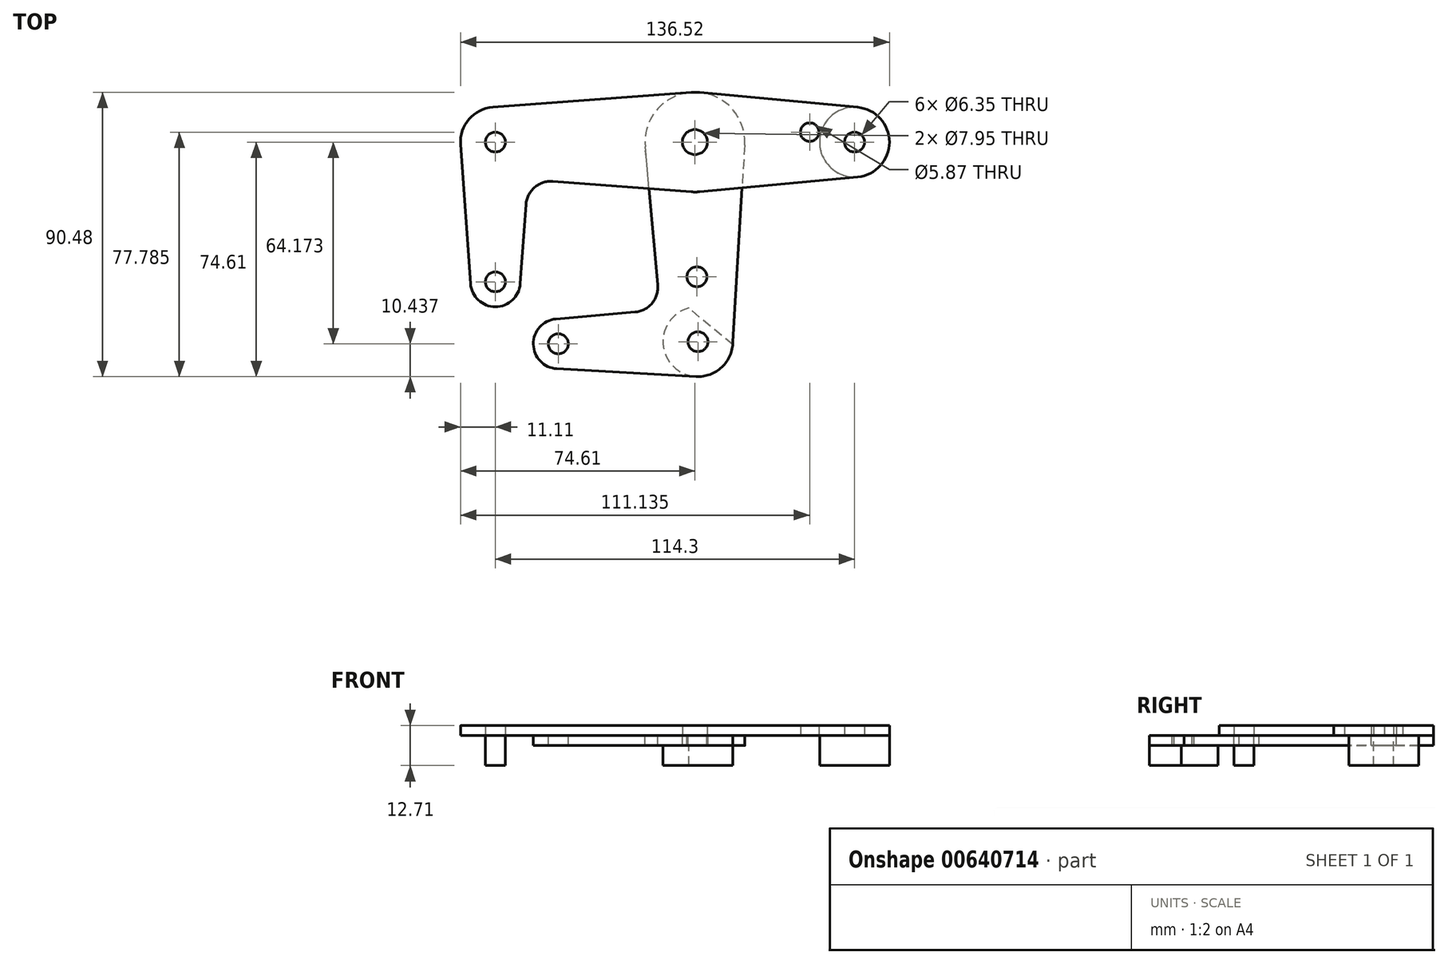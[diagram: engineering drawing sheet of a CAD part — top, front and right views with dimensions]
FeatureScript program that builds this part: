
annotation { "Feature Type Name" : "Feature", "Feature Type Description" : "" }
export const myFeature = defineFeature(function(context is Context, id is Id, definition is map)
    precondition{}
    {
        {
            var Q0;
            Q0=qCreatedBy(makeId("Top.planeOp"),FACE);
            var sketch = newSketch(context, id + "F0", { "sketchPlane" : qUnion([Q0])});
            skCircle(sketch, "E0", {"center": v(-63.5, -44.45) * mm, "radius": 3.18 * mm});
            skCircle(sketch, "E1", {"center": v(-63.5, -44.45) * mm, "radius": 7.94 * mm});
            skCircle(sketch, "E2", {"center": v(-63.5, 0) * mm, "radius": 3.18 * mm});
            skCircle(sketch, "E3", {"center": v(-63.5, 0) * mm, "radius": 11.11 * mm});
            skCircle(sketch, "E4", {"center": v(0, 0) * mm, "radius": 2.94 * mm});
            skCircle(sketch, "E5", {"center": v(0, 0) * mm, "radius": 3.98 * mm});
            skCircle(sketch, "E6", {"center": v(0, 0) * mm, "radius": 15.88 * mm});
            skLineSegment(sketch, "E7", {"start": v(-71.42, -45.02) * mm, "end": v(-74.58, -0.8) * mm});
            skLineSegment(sketch, "E8", {"start": v(-64.33, 11.08) * mm, "end": v(-1.2, 15.83) * mm});
            skLineSegment(sketch, "E9", {"start": v(-53.78, -19.88) * mm, "end": v(-55.58, -45.02) * mm});
            skLineSegment(sketch, "E10", {"start": v(-1.2, -15.83) * mm, "end": v(-45.26, -12.52) * mm});
            skArc(sketch, "E11", {"start": v(-45.26, -12.52) * mm, "mid": v(-51.05, -14.43) * mm, "end": v(-53.78, -19.88) * mm});
            skLineSegment(sketch, "E12", {"start": v(-63.5, 0) * mm, "end": v(-63.5, -44.45) * mm, "construction": true});
            skCircle(sketch, "E13", {"center": v(0.96, -63.5) * mm, "radius": 11.11 * mm});
            skCircle(sketch, "E14", {"center": v(0.96, -63.5) * mm, "radius": 3.18 * mm});
            skCircle(sketch, "E15", {"center": v(-43.49, -64.17) * mm, "radius": 7.94 * mm});
            skCircle(sketch, "E16", {"center": v(-43.49, -64.17) * mm, "radius": 3.18 * mm});
            skLineSegment(sketch, "E17", {"start": v(15.85, -0.96) * mm, "end": v(12.07, -63.5) * mm});
            skLineSegment(sketch, "E18", {"start": v(0.34, -74.6) * mm, "end": v(-43.94, -72.1) * mm});
            skCircle(sketch, "E19", {"center": v(0.65, -42.85) * mm, "radius": 3.18 * mm});
            skLineSegment(sketch, "E20", {"start": v(0, 0) * mm, "end": v(0.96, -63.5) * mm, "construction": true});
            skLineSegment(sketch, "E21", {"start": v(0.96, -63.5) * mm, "end": v(-43.49, -64.17) * mm, "construction": true});
            skLineSegment(sketch, "E22", {"start": v(-63.5, 0) * mm, "end": v(50.8, 0) * mm, "construction": true});
            skCircle(sketch, "E23", {"center": v(50.8, 0) * mm, "radius": 11.11 * mm});
            skLineSegment(sketch, "E24", {"start": v(1.49, 15.8) * mm, "end": v(51.84, 11.06) * mm});
            skLineSegment(sketch, "E25", {"start": v(1.49, -15.8) * mm, "end": v(51.84, -11.06) * mm});
            skCircle(sketch, "E26", {"center": v(36.53, 3.17) * mm, "radius": 2.94 * mm});
            skLineSegment(sketch, "E27", {"start": v(36.53, 0) * mm, "end": v(36.53, 3.17) * mm, "construction": true});
            skCircle(sketch, "E28", {"center": v(50.8, 0) * mm, "radius": 3.18 * mm});
            skLineSegment(sketch, "E29", {"start": v(0, -52.43) * mm, "end": v(0, -52.43) * mm});
            skArc(sketch, "E30", {"start": v(-19.06, -54.08) * mm, "mid": v(-13.65, -51.27) * mm, "end": v(-11.83, -45.45) * mm});
            skLineSegment(sketch, "E31.trimOffspring", {"start": v(-19.06, -54.08) * mm, "end": v(-44.18, -56.27) * mm});
            skLineSegment(sketch, "E32", {"start": v(-11.83, -45.45) * mm, "end": v(-15.81, -1.43) * mm});
            skSolve(sketch);
        }
        {
            var Q0;
            {var subQ0=sQuery(id+"F0.wireOp",EDGE,"E10");var subQ1=sQuery(id+"F0.wireOp",EDGE,"E6");var subQ2=makeQuery(id+"F0.imprint","INTERSECT",VERTEX,{"derivedFrom":[subQ1,subQ0]});Q0=makeQuery(id+"F0.imprint","IMPRINT",FACE,{"disambiguationData":[TD([[makeQuery(id+"F0.imprint","IMPRINT",EDGE,{"disambiguationData":[TD([[subQ2,1.0]])],"derivedFrom":subQ1}),-1.0]])]});}
            var Q1;
            Q1=makeQuery(id+"F0.imprint","IMPRINT",FACE,{"disambiguationData":[TD([[makeQuery(id+"F0.imprint","IMPRINT",EDGE,{"derivedFrom":sQuery(id+"F0.wireOp",EDGE,"E5")}),-1.0]])]});
            var Q2;
            {var subQ0=sQuery(id+"F0.wireOp",EDGE,"E17");var subQ1=sQuery(id+"F0.wireOp",EDGE,"E6");var subQ2=makeQuery(id+"F0.imprint","INTERSECT",VERTEX,{"derivedFrom":[subQ1,subQ0]});Q2=makeQuery(id+"F0.imprint","IMPRINT",FACE,{"disambiguationData":[TD([[makeQuery(id+"F0.imprint","IMPRINT",EDGE,{"disambiguationData":[TD([[subQ2,1.0]])],"derivedFrom":subQ1}),-1.0]])]});}
            var Q3;
            {var subQ0=sQuery(id+"F0.wireOp",EDGE,"E24");Q3=makeQuery(id+"F0.imprint","IMPRINT",FACE,{"disambiguationData":[TD([[makeQuery(id+"F0.imprint","IMPRINT",EDGE,{"derivedFrom":subQ0}),-1.0]])]});}
            var Q4;
            Q4=makeQuery(id+"F0.imprint","IMPRINT",FACE,{"disambiguationData":[TD([[makeQuery(id+"F0.imprint","IMPRINT",EDGE,{"derivedFrom":sQuery(id+"F0.wireOp",EDGE,"E28")}),-1.0]])]});
            var Q5;
            {var subQ0=sQuery(id+"F0.wireOp",EDGE,"E7");Q5=makeQuery(id+"F0.imprint","IMPRINT",FACE,{"disambiguationData":[TD([[makeQuery(id+"F0.imprint","IMPRINT",EDGE,{"derivedFrom":subQ0}),-1.0]])]});}
            var Q6;
            Q6=makeQuery(id+"F0.imprint","IMPRINT",FACE,{"disambiguationData":[TD([[makeQuery(id+"F0.imprint","IMPRINT",EDGE,{"derivedFrom":sQuery(id+"F0.wireOp",EDGE,"E0")}),-1.0]])]});
            var Q7;
            Q7=makeQuery(id+"F0.imprint","IMPRINT",FACE,{"disambiguationData":[TD([[makeQuery(id+"F0.imprint","IMPRINT",EDGE,{"derivedFrom":sQuery(id+"F0.wireOp",EDGE,"E2")}),-1.0]])]});
            extrude(context, id + "F1", {"entities" : qUnion([Q0, Q1, Q2, Q3, Q4, Q5, Q6, Q7]), "depth" : 3.17 * mm, "offsetDistance" : 25.4 * mm});
        }
        {
            var Q0;
            {var subQ11=sQuery(id+"F0.wireOp",EDGE,"E18");Q0=makeQuery(id+"F0.imprint","IMPRINT",FACE,{"disambiguationData":[TD([[makeQuery(id+"F0.imprint","IMPRINT",EDGE,{"derivedFrom":subQ11}),-1.0]])]});}
            var Q1;
            Q1=makeQuery(id+"F0.imprint","IMPRINT",FACE,{"disambiguationData":[TD([[makeQuery(id+"F0.imprint","IMPRINT",EDGE,{"derivedFrom":sQuery(id+"F0.wireOp",EDGE,"E14")}),-1.0]])]});
            var Q2;
            Q2=makeQuery(id+"F0.imprint","IMPRINT",FACE,{"disambiguationData":[TD([[makeQuery(id+"F0.imprint","IMPRINT",EDGE,{"derivedFrom":sQuery(id+"F0.wireOp",EDGE,"E16")}),-1.0]])]});
            var Q3;
            {var subQ0=sQuery(id+"F0.wireOp",EDGE,"E17");var subQ1=sQuery(id+"F0.wireOp",EDGE,"E6");var subQ2=makeQuery(id+"F0.imprint","INTERSECT",VERTEX,{"derivedFrom":[subQ1,subQ0]});Q3=makeQuery(id+"F0.imprint","IMPRINT",FACE,{"disambiguationData":[TD([[makeQuery(id+"F0.imprint","IMPRINT",EDGE,{"disambiguationData":[TD([[subQ2,1.0]])],"derivedFrom":subQ1}),-1.0]])]});}
            var Q4;
            Q4=makeQuery(id+"F0.imprint","IMPRINT",FACE,{"disambiguationData":[TD([[makeQuery(id+"F0.imprint","IMPRINT",EDGE,{"derivedFrom":sQuery(id+"F0.wireOp",EDGE,"E5")}),-1.0]])]});
            var Q5;
            {var subQ0=sQuery(id+"F0.wireOp",EDGE,"E10");var subQ1=sQuery(id+"F0.wireOp",EDGE,"E6");var subQ2=makeQuery(id+"F0.imprint","INTERSECT",VERTEX,{"derivedFrom":[subQ1,subQ0]});Q5=makeQuery(id+"F0.imprint","IMPRINT",FACE,{"disambiguationData":[TD([[makeQuery(id+"F0.imprint","IMPRINT",EDGE,{"disambiguationData":[TD([[subQ2,1.0]])],"derivedFrom":subQ1}),-1.0]])]});}
            extrude(context, id + "F2", {"entities" : qUnion([Q0, Q1, Q2, Q3, Q4, Q5]), "oppositeDirection" : true, "depth" : 3.17 * mm, "offsetDistance" : 25.4 * mm});
        }
        {
            var Q0;
            Q0=makeQuery(id+"F2.opExtrude","CAP_FACE",FACE,{"disambiguationData":[OSD([sQuery(id+"F0.wireOp",EDGE,"E5"),sQuery(id+"F0.wireOp",EDGE,"E6"),sQuery(id+"F0.wireOp",EDGE,"E13"),sQuery(id+"F0.wireOp",EDGE,"E14"),sQuery(id+"F0.wireOp",EDGE,"E15"),sQuery(id+"F0.wireOp",EDGE,"E16"),sQuery(id+"F0.wireOp",EDGE,"E17"),sQuery(id+"F0.wireOp",EDGE,"E18"),sQuery(id+"F0.wireOp",EDGE,"E19"),sQuery(id+"F0.wireOp",EDGE,"E30"),sQuery(id+"F0.wireOp",EDGE,"E31.trimOffspring"),sQuery(id+"F0.wireOp",EDGE,"E32")])],"isStart":true});
            var sketch = newSketch(context, id + "F3", { "sketchPlane" : qUnion([Q0])});
            skArc(sketch, "E33", {"start": v(-1.97, -52.78) * mm, "mid": v(-6.16, -72.03) * mm, "end": v(12.03, -64.47) * mm});
            skLineSegment(sketch, "E34", {"start": v(-1.97, -52.78) * mm, "end": v(12.07, -64.5) * mm});
            skPoint(sketch, "E35.orphan", {"position": v(54, 0) * mm});
            skSolve(sketch);
        }
        {
            var Q0;
            Q0=qCreatedBy(makeId("Top.planeOp"),FACE);
            cPlane(context, id + "F4", {"entities" : qUnion([Q0]), "cplaneType" : CPlaneType.OFFSET, "offset" : 9.52 * mm, "oppositeDirection" : true, "width" : 152.4 * mm, "height" : 152.4 * mm});
        }
        {
            var Q0;
            Q0=makeQuery(id+"F1.opExtrude","CAP_FACE",FACE,{"disambiguationData":[OSD([sQuery(id+"F0.wireOp",EDGE,"E0"),sQuery(id+"F0.wireOp",EDGE,"E1"),sQuery(id+"F0.wireOp",EDGE,"E2"),sQuery(id+"F0.wireOp",EDGE,"E3"),sQuery(id+"F0.wireOp",EDGE,"E5"),sQuery(id+"F0.wireOp",EDGE,"E6"),sQuery(id+"F0.wireOp",EDGE,"E7"),sQuery(id+"F0.wireOp",EDGE,"E8"),sQuery(id+"F0.wireOp",EDGE,"E9"),sQuery(id+"F0.wireOp",EDGE,"E10"),sQuery(id+"F0.wireOp",EDGE,"E11"),sQuery(id+"F0.wireOp",EDGE,"E23"),sQuery(id+"F0.wireOp",EDGE,"E24"),sQuery(id+"F0.wireOp",EDGE,"E25"),sQuery(id+"F0.wireOp",EDGE,"E26"),sQuery(id+"F0.wireOp",EDGE,"E28")])],"isStart":false});
            var sketch = newSketch(context, id + "F5", { "sketchPlane" : qUnion([Q0])});
            skCircle(sketch, "E36", {"center": v(50.8, 0) * mm, "radius": 11.11 * mm});
            skSolve(sketch);
        }
        {
            var Q0;
            Q0 = qSketchRegion(id + "F3", true);
            var Q1;
            Q1=makeQuery(id+"F0.imprint","IMPRINT",FACE,{"disambiguationData":[TD([[makeQuery(id+"F0.imprint","IMPRINT",EDGE,{"derivedFrom":sQuery(id+"F0.wireOp",EDGE,"E28")}),-1.0]])]});
            var Q2;
            Q2=makeQuery(id+"F0.imprint","IMPRINT",FACE,{"disambiguationData":[TD([[makeQuery(id+"F0.imprint","IMPRINT",EDGE,{"derivedFrom":sQuery(id+"F0.wireOp",EDGE,"E28")}),1.0]])]});
            var Q3;
            Q3=makeQuery(id+"F0.imprint","IMPRINT",FACE,{"disambiguationData":[TD([[makeQuery(id+"F0.imprint","IMPRINT",EDGE,{"derivedFrom":sQuery(id+"F0.wireOp",EDGE,"E0")}),1.0]])]});
            var Q4;
            Q4=makeQuery(id+"F0.imprint","IMPRINT",FACE,{"disambiguationData":[TD([[makeQuery(id+"F0.imprint","IMPRINT",EDGE,{"derivedFrom":sQuery(id+"F0.wireOp",EDGE,"E2")}),1.0]])]});
            var Q5;
            Q5=qCreatedBy(id+"F4.planeOp",FACE);
            extrude(context, id + "F6", {"entities" : qUnion([Q0, Q1, Q2, Q3, Q4]), "endBound" : BoundingType.UP_TO_SURFACE, "oppositeDirection" : true, "depth" : 10.16 * mm, "endBoundEntityFace" : qUnion([Q5]), "offsetDistance" : 25.4 * mm});
        }
        {
            var Q0;
            Q0=makeQuery(id+"F2.opExtrude","SWEPT_BODY",BODY,{"disambiguationData":[OSD([sQuery(id+"F0.wireOp",EDGE,"E5"),sQuery(id+"F0.wireOp",EDGE,"E6"),sQuery(id+"F0.wireOp",EDGE,"E13"),sQuery(id+"F0.wireOp",EDGE,"E14"),sQuery(id+"F0.wireOp",EDGE,"E15"),sQuery(id+"F0.wireOp",EDGE,"E16"),sQuery(id+"F0.wireOp",EDGE,"E17"),sQuery(id+"F0.wireOp",EDGE,"E18"),sQuery(id+"F0.wireOp",EDGE,"E19"),sQuery(id+"F0.wireOp",EDGE,"E30"),sQuery(id+"F0.wireOp",EDGE,"E31.trimOffspring"),sQuery(id+"F0.wireOp",EDGE,"E32")])]});
            var Q1;
            Q1=makeQuery(id+"F6.opExtrude","SWEPT_BODY",BODY,{"disambiguationData":[OSD([sQuery(id+"F3.wireOp",EDGE,"E33"),sQuery(id+"F3.wireOp",EDGE,"E34")])]});
            booleanBodies(context, id + "F7", {"operationType" : BooleanOperationType.SUBTRACTION, "tools" : qUnion([Q0]), "targets" : qUnion([Q1]), "keepTools" : true});
        }
    });
